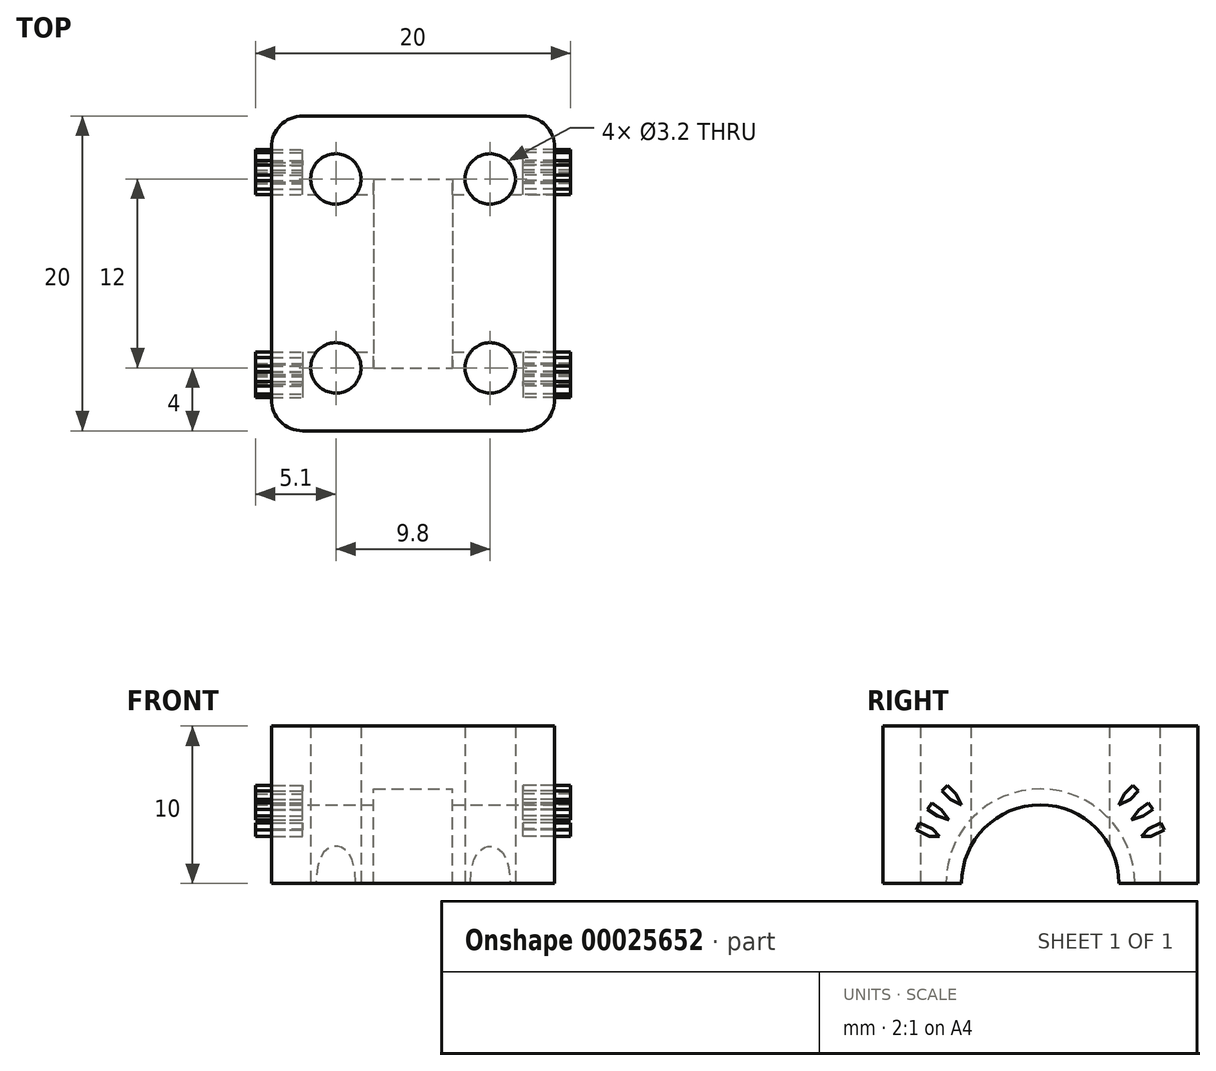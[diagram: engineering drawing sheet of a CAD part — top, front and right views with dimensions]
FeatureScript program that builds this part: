
annotation { "Feature Type Name" : "Feature", "Feature Type Description" : "" }
export const myFeature = defineFeature(function(context is Context, id is Id, definition is map)
    precondition{}
    {
        {
            var Q0;
            Q0=qCreatedBy(makeId("Top.planeOp"),FACE);
            var sketch = newSketch(context, id + "F0", { "sketchPlane" : qUnion([Q0])});
            skLineSegment(sketch, "E0.rect.bottom", {"start": v(4.9, -6) * mm, "end": v(-4.9, -6) * mm, "construction": true});
            skLineSegment(sketch, "E0.rect.top", {"start": v(4.9, 6) * mm, "end": v(-4.9, 6) * mm, "construction": true});
            skLineSegment(sketch, "E0.rect.left", {"start": v(4.9, -6) * mm, "end": v(4.9, 6) * mm, "construction": true});
            skLineSegment(sketch, "E0.rect.right", {"start": v(-4.9, -6) * mm, "end": v(-4.9, 6) * mm, "construction": true});
            skPoint(sketch, "E0.rect.middle", {"position": v(0, 0) * mm});
            skCircle(sketch, "E1", {"center": v(-4.9, 6) * mm, "radius": 1.6 * mm});
            skCircle(sketch, "E2.0.MirrorC", {"center": v(4.9, 6) * mm, "radius": 1.6 * mm});
            skCircle(sketch, "E3.0.MirrorC", {"center": v(-4.9, -6) * mm, "radius": 1.6 * mm});
            skCircle(sketch, "E4.0.MirrorC", {"center": v(4.9, -6) * mm, "radius": 1.6 * mm});
            skLineSegment(sketch, "E5.rect.bottom", {"start": v(-12.29, 4) * mm, "end": v(12.29, 4) * mm, "construction": true});
            skLineSegment(sketch, "E5.rect.top", {"start": v(-12.29, -4) * mm, "end": v(12.29, -4) * mm, "construction": true});
            skLineSegment(sketch, "E6.rect.bottom", {"start": v(7, -10) * mm, "end": v(-7, -10) * mm});
            skLineSegment(sketch, "E6.rect.top", {"start": v(7, 10) * mm, "end": v(-7, 10) * mm});
            skLineSegment(sketch, "E6.rect.left", {"start": v(9, -8) * mm, "end": v(9, 8) * mm});
            skLineSegment(sketch, "E6.rect.right", {"start": v(-9, -8) * mm, "end": v(-9, 8) * mm});
            skPoint(sketch, "E7.visualSharp", {"position": v(-9, 10) * mm});
            skArc(sketch, "E7.filletArc", {"start": v(-7, 10) * mm, "mid": v(-8.41, 9.41) * mm, "end": v(-9, 8) * mm});
            skPoint(sketch, "E8.visualSharp", {"position": v(9, 10) * mm});
            skArc(sketch, "E8.filletArc", {"start": v(9, 8) * mm, "mid": v(8.41, 9.41) * mm, "end": v(7, 10) * mm});
            skPoint(sketch, "E9.visualSharp", {"position": v(9, -10) * mm});
            skArc(sketch, "E9.filletArc", {"start": v(7, -10) * mm, "mid": v(8.41, -9.41) * mm, "end": v(9, -8) * mm});
            skPoint(sketch, "E10.visualSharp", {"position": v(-9, -10) * mm});
            skArc(sketch, "E10.filletArc", {"start": v(-9, -8) * mm, "mid": v(-8.41, -9.41) * mm, "end": v(-7, -10) * mm});
            skSolve(sketch);
        }
        {
            var Q0;
            Q0=qSketchRegion(id+"F0",true);
            extrude(context, id + "F1", {"entities" : qUnion([Q0]), "depth" : 10 * mm});
        }
        {
            var Q0;
            Q0=qCreatedBy(makeId("Front.planeOp"),FACE);
            var sketch = newSketch(context, id + "F2", { "sketchPlane" : qUnion([Q0])});
            skLineSegment(sketch, "E11", {"start": v(0, 0) * mm, "end": v(11.21, 0) * mm, "construction": true});
            skLineSegment(sketch, "E12", {"start": v(0, 0) * mm, "end": v(-12.6, 0) * mm, "construction": true});
            skLineSegment(sketch, "E13", {"start": v(-9.87, 0) * mm, "end": v(-9.87, 5) * mm});
            skLineSegment(sketch, "E14", {"start": v(-9.87, 5) * mm, "end": v(-2.5, 5) * mm});
            skLineSegment(sketch, "E15", {"start": v(-2.5, 5) * mm, "end": v(-2.5, 6) * mm});
            skLineSegment(sketch, "E16", {"start": v(-2.5, 6) * mm, "end": v(0, 6) * mm});
            skLineSegment(sketch, "E17", {"start": v(0, 0) * mm, "end": v(-9.87, 0) * mm});
            skLineSegment(sketch, "E18", {"start": v(0, 0) * mm, "end": v(0, 13.48) * mm, "construction": true});
            skLineSegment(sketch, "E19.0.MirrorCS", {"start": v(2.5, 6) * mm, "end": v(0, 6) * mm});
            skLineSegment(sketch, "E20.0.MirrorCS", {"start": v(2.5, 5) * mm, "end": v(2.5, 6) * mm});
            skLineSegment(sketch, "E21.0.MirrorCS", {"start": v(9.87, 5) * mm, "end": v(2.5, 5) * mm});
            skLineSegment(sketch, "E22.0.MirrorCS", {"start": v(9.87, 0) * mm, "end": v(9.87, 5) * mm});
            skLineSegment(sketch, "E23.0.MirrorCS", {"start": v(0, 0) * mm, "end": v(9.87, 0) * mm});
            skSolve(sketch);
        }
        {
            var Q0;
            Q0=makeQuery(id+"F2.imprint","IMPRINT",FACE,{"disambiguationData":[TD([[makeQuery(id+"F2.imprint","IMPRINT",EDGE,{"derivedFrom":sQuery(id+"F2.wireOp",EDGE,"E13")}),-1.0]])]});
            var Q1;
            Q1=sQuery(id+"F2.wireOp",EDGE,"E12");
            revolve(context, id + "F3", {"entities" : qUnion([Q0]), "axis" : qUnion([Q1]), "revolveType" : RevolveType.FULL});
        }
        {
            var Q0;
            Q0=makeQuery(id+"F3.opRevolve","SWEPT_BODY",BODY,{"disambiguationData":[OSD([sQuery(id+"F2.wireOp",EDGE,"E13"),sQuery(id+"F2.wireOp",EDGE,"E14"),sQuery(id+"F2.wireOp",EDGE,"E15"),sQuery(id+"F2.wireOp",EDGE,"E16"),sQuery(id+"F2.wireOp",EDGE,"E17"),sQuery(id+"F2.wireOp",EDGE,"E19.0.MirrorCS"),sQuery(id+"F2.wireOp",EDGE,"E20.0.MirrorCS"),sQuery(id+"F2.wireOp",EDGE,"E21.0.MirrorCS"),sQuery(id+"F2.wireOp",EDGE,"E22.0.MirrorCS"),sQuery(id+"F2.wireOp",EDGE,"E23.0.MirrorCS")])]});
            var Q1;
            Q1=makeQuery(id+"F1.opExtrude","SWEPT_BODY",BODY,{"disambiguationData":[OSD([sQuery(id+"F0.wireOp",EDGE,"E1"),sQuery(id+"F0.wireOp",EDGE,"E2.0.MirrorC"),sQuery(id+"F0.wireOp",EDGE,"E3.0.MirrorC"),sQuery(id+"F0.wireOp",EDGE,"E4.0.MirrorC"),sQuery(id+"F0.wireOp",EDGE,"e5631a11-bc9c-4a52-adc7-c46cd8f11f6b"),sQuery(id+"F0.wireOp",EDGE,"bd637b92-1d0b-446d-8915-1d70d333add2.0.MirrorCS"),sQuery(id+"F0.wireOp",EDGE,"06c50760-1331-4ed2-a7b0-091f787a3063"),sQuery(id+"F0.wireOp",EDGE,"de07cfb3-cb16-40ab-bb82-3127aa1393aa"),sQuery(id+"F0.wireOp",EDGE,"04999754-2a12-4e44-a85a-65a4e2ceeff6"),sQuery(id+"F0.wireOp",EDGE,"dadc4557-2f52-4a31-bb1e-40eb43539002"),sQuery(id+"F0.wireOp",EDGE,"8e725be4-5807-46b2-9b6e-bd76df486bfe"),sQuery(id+"F0.wireOp",EDGE,"98050970-c6e9-4b0a-98d8-9d9cee821ab9"),sQuery(id+"F0.wireOp",EDGE,"6ad0ad36-7af7-4ad4-b520-2d92bf48e3fd"),sQuery(id+"F0.wireOp",EDGE,"b438de05-f02d-4cf3-920c-0279d859b767"),sQuery(id+"F0.wireOp",EDGE,"d851b83f-9951-4aca-81a3-513ac486d921"),sQuery(id+"F0.wireOp",EDGE,"5981cd49-f631-4702-ace7-539b31d2d0b1"),sQuery(id+"F0.wireOp",EDGE,"dddef0f6-cba6-4fc5-84df-45972f3e2711.filletArc"),sQuery(id+"F0.wireOp",EDGE,"58242231-5e53-4480-9a1e-0624a7f1f4e7.filletArc"),sQuery(id+"F0.wireOp",EDGE,"b5da0da3-f109-4bb3-8592-48b764635490.filletArc"),sQuery(id+"F0.wireOp",EDGE,"02dcfeaf-069a-4237-823f-dfffc468ed8a.filletArc")])]});
            booleanBodies(context, id + "F4", {"operationType" : BooleanOperationType.SUBTRACTION, "tools" : qUnion([Q0]), "targets" : qUnion([Q1])});
        }
        {
            var Q0;
            Q0=qCreatedBy(makeId("Right.planeOp"),FACE);
            var sketch = newSketch(context, id + "F5", { "sketchPlane" : qUnion([Q0])});
            skLineSegment(sketch, "E24.rect.bottom", {"start": v(5, -5) * mm, "end": v(-5, -5) * mm, "construction": true});
            skLineSegment(sketch, "E24.rect.top", {"start": v(5, 5) * mm, "end": v(-5, 5) * mm, "construction": true});
            skLineSegment(sketch, "E24.rect.left", {"start": v(5, -5) * mm, "end": v(5, 5) * mm, "construction": true});
            skLineSegment(sketch, "E24.rect.right", {"start": v(-5, -5) * mm, "end": v(-5, 5) * mm, "construction": true});
            skPoint(sketch, "E24.rect.middle", {"position": v(0, 0) * mm});
            skLineSegment(sketch, "E25", {"start": v(0, 0) * mm, "end": v(-6.64, 6.64) * mm, "construction": true});
            skLineSegment(sketch, "E26", {"start": v(0, 0) * mm, "end": v(-5.8, 4.06) * mm, "construction": true});
            skLineSegment(sketch, "E27", {"start": v(0, 0) * mm, "end": v(-5.42, 4.55) * mm, "construction": true});
            skLineSegment(sketch, "E28", {"start": v(0, 0) * mm, "end": v(-6.12, 3.54) * mm, "construction": true});
            skLineSegment(sketch, "E29", {"start": v(0, 0) * mm, "end": v(-6.4, 2.99) * mm, "construction": true});
            skLineSegment(sketch, "E30", {"start": v(0, 0) * mm, "end": v(-5, 5) * mm});
            skLineSegment(sketch, "E31", {"start": v(0, 0) * mm, "end": v(-6.29, 7.92) * mm, "construction": true});
            skLineSegment(sketch, "E32", {"start": v(0, 0) * mm, "end": v(0, 0.41) * mm, "construction": true});
            skLineSegment(sketch, "E33", {"start": v(-5, 5) * mm, "end": v(-6.06, 6.06) * mm});
            skLineSegment(sketch, "E34", {"start": v(-5.8, 4.06) * mm, "end": v(-7.02, 4.92) * mm});
            skLineSegment(sketch, "E35", {"start": v(-6.4, 2.99) * mm, "end": v(-7.77, 3.62) * mm});
            skLineSegment(sketch, "E36.0", {"start": v(-5.35, 5.7) * mm, "end": v(-5.88, 6.24) * mm});
            skLineSegment(sketch, "E37.0", {"start": v(-5.7, 5.35) * mm, "end": v(-6.24, 5.88) * mm});
            skLineSegment(sketch, "E38", {"start": v(-5.88, 6.24) * mm, "end": v(-6.24, 5.88) * mm});
            skLineSegment(sketch, "E39", {"start": v(-5, 5) * mm, "end": v(-5.35, 5.7) * mm});
            skLineSegment(sketch, "E40", {"start": v(-5, 5) * mm, "end": v(-5.7, 5.35) * mm});
            skLineSegment(sketch, "E41", {"start": v(-5.42, 4.55) * mm, "end": v(-5.46, 4.59) * mm});
            skLineSegment(sketch, "E42", {"start": v(0, 0) * mm, "end": v(0, 8.3) * mm, "construction": true});
            skLineSegment(sketch, "E43.0.MirrorCS", {"start": v(5.35, 5.7) * mm, "end": v(5.88, 6.24) * mm});
            skLineSegment(sketch, "E44.0.MirrorCS", {"start": v(5.7, 5.35) * mm, "end": v(6.24, 5.88) * mm});
            skLineSegment(sketch, "E45.0.MirrorCS", {"start": v(5.88, 6.24) * mm, "end": v(6.24, 5.88) * mm});
            skLineSegment(sketch, "E46.0.MirrorCS", {"start": v(5, 5) * mm, "end": v(5.7, 5.35) * mm});
            skLineSegment(sketch, "E47.0.MirrorCS", {"start": v(5, 5) * mm, "end": v(5.35, 5.7) * mm});
            skLineSegment(sketch, "E48.0", {"start": v(-6.26, 4.7) * mm, "end": v(-6.88, 5.12) * mm});
            skLineSegment(sketch, "E49.0", {"start": v(-6.55, 4.28) * mm, "end": v(-7.16, 4.71) * mm});
            skLineSegment(sketch, "E50", {"start": v(-5.8, 4.06) * mm, "end": v(-6.26, 4.7) * mm});
            skLineSegment(sketch, "E51", {"start": v(-5.8, 4.06) * mm, "end": v(-6.55, 4.28) * mm});
            skLineSegment(sketch, "E52", {"start": v(-7.16, 4.71) * mm, "end": v(-6.88, 5.12) * mm});
            skPoint(sketch, "E53.orphan", {"position": v(-6.25, 3.32) * mm});
            skPoint(sketch, "E54.orphan", {"position": v(-6, 3.75) * mm});
            skLineSegment(sketch, "E55.0.MirrorCS", {"start": v(6.26, 4.7) * mm, "end": v(6.88, 5.12) * mm});
            skLineSegment(sketch, "E56.0.MirrorCS", {"start": v(6.55, 4.28) * mm, "end": v(7.16, 4.71) * mm});
            skLineSegment(sketch, "E57.0.MirrorCS", {"start": v(7.16, 4.71) * mm, "end": v(6.88, 5.12) * mm});
            skLineSegment(sketch, "E58.0.MirrorCS", {"start": v(5.8, 4.06) * mm, "end": v(6.55, 4.28) * mm});
            skLineSegment(sketch, "E59.0.MirrorCS", {"start": v(5.8, 4.06) * mm, "end": v(6.26, 4.7) * mm});
            skLineSegment(sketch, "E60.0", {"start": v(-6.85, 3.47) * mm, "end": v(-7.66, 3.85) * mm});
            skLineSegment(sketch, "E61.0", {"start": v(-7.03, 3) * mm, "end": v(-7.87, 3.4) * mm});
            skLineSegment(sketch, "E62", {"start": v(-7.66, 3.85) * mm, "end": v(-7.87, 3.4) * mm});
            skLineSegment(sketch, "E63", {"start": v(-6.4, 2.99) * mm, "end": v(-6.85, 3.47) * mm});
            skLineSegment(sketch, "E64", {"start": v(-6.4, 2.99) * mm, "end": v(-7.03, 3) * mm});
            skLineSegment(sketch, "E65.0.MirrorCS", {"start": v(6.85, 3.47) * mm, "end": v(7.66, 3.85) * mm});
            skLineSegment(sketch, "E66.0.MirrorCS", {"start": v(7.66, 3.85) * mm, "end": v(7.87, 3.4) * mm});
            skLineSegment(sketch, "E67.0.MirrorCS", {"start": v(7.03, 3) * mm, "end": v(7.87, 3.4) * mm});
            skLineSegment(sketch, "E68.0.MirrorCS", {"start": v(6.4, 2.99) * mm, "end": v(7.03, 3) * mm});
            skLineSegment(sketch, "E69.0.MirrorCS", {"start": v(6.4, 2.99) * mm, "end": v(6.85, 3.47) * mm});
            skSolve(sketch);
        }
        {
            var Q0;
            Q0=qSketchRegion(id+"F5",true);
            extrude(context, id + "F6", {"entities" : qUnion([Q0]), "depth" : 3 * mm});
        }
        {
            var Q0;
            Q0=makeQuery(id+"F6.opExtrude","SWEPT_BODY",BODY,{"disambiguationData":[OSD([sQuery(id+"F5.wireOp",EDGE,"E60.0"),sQuery(id+"F5.wireOp",EDGE,"E61.0"),sQuery(id+"F5.wireOp",EDGE,"E62"),sQuery(id+"F5.wireOp",EDGE,"E63"),sQuery(id+"F5.wireOp",EDGE,"E64")])]});
            var Q1;
            Q1=makeQuery(id+"F6.opExtrude","SWEPT_BODY",BODY,{"disambiguationData":[OSD([sQuery(id+"F5.wireOp",EDGE,"E48.0"),sQuery(id+"F5.wireOp",EDGE,"E49.0"),sQuery(id+"F5.wireOp",EDGE,"E50"),sQuery(id+"F5.wireOp",EDGE,"E51"),sQuery(id+"F5.wireOp",EDGE,"E52")])]});
            var Q2;
            Q2=makeQuery(id+"F6.opExtrude","SWEPT_BODY",BODY,{"disambiguationData":[OSD([sQuery(id+"F5.wireOp",EDGE,"E36.0"),sQuery(id+"F5.wireOp",EDGE,"E37.0"),sQuery(id+"F5.wireOp",EDGE,"E38"),sQuery(id+"F5.wireOp",EDGE,"E39"),sQuery(id+"F5.wireOp",EDGE,"E40")])]});
            var Q3;
            Q3=makeQuery(id+"F6.opExtrude","SWEPT_BODY",BODY,{"disambiguationData":[OSD([sQuery(id+"F5.wireOp",EDGE,"E43.0.MirrorCS"),sQuery(id+"F5.wireOp",EDGE,"E44.0.MirrorCS"),sQuery(id+"F5.wireOp",EDGE,"E45.0.MirrorCS"),sQuery(id+"F5.wireOp",EDGE,"E46.0.MirrorCS"),sQuery(id+"F5.wireOp",EDGE,"E47.0.MirrorCS")])]});
            var Q4;
            Q4=makeQuery(id+"F6.opExtrude","SWEPT_BODY",BODY,{"disambiguationData":[OSD([sQuery(id+"F5.wireOp",EDGE,"E65.0.MirrorCS"),sQuery(id+"F5.wireOp",EDGE,"E66.0.MirrorCS"),sQuery(id+"F5.wireOp",EDGE,"E67.0.MirrorCS"),sQuery(id+"F5.wireOp",EDGE,"E68.0.MirrorCS"),sQuery(id+"F5.wireOp",EDGE,"E69.0.MirrorCS")])]});
            var Q5;
            Q5=makeQuery(id+"F6.opExtrude","SWEPT_BODY",BODY,{"disambiguationData":[OSD([sQuery(id+"F5.wireOp",EDGE,"E55.0.MirrorCS"),sQuery(id+"F5.wireOp",EDGE,"E56.0.MirrorCS"),sQuery(id+"F5.wireOp",EDGE,"E57.0.MirrorCS"),sQuery(id+"F5.wireOp",EDGE,"E58.0.MirrorCS"),sQuery(id+"F5.wireOp",EDGE,"E59.0.MirrorCS")])]});
            var Q6;
            Q6=makeQuery(id+"F1.opExtrude","SWEPT_FACE",FACE,{"disambiguationData":[OSD([sQuery(id+"F0.wireOp",EDGE,"E6.rect.left")])]});
            transform(context, id + "F7", {"entities" : qUnion([Q0, Q1, Q2, Q3, Q4, Q5]), "transformType" : TransformType.TRANSLATION_DISTANCE, "transformDirection" : qUnion([Q6]), "distance" : 7 * mm, "makeCopy" : false});
        }
        {
            var Q0;
            Q0=qSketchRegion(id+"F5",true);
            extrude(context, id + "F8", {"entities" : qUnion([Q0]), "oppositeDirection" : true, "depth" : 3 * mm});
        }
        {
            var Q0;
            Q0=makeQuery(id+"F8.opExtrude","SWEPT_BODY",BODY,{"disambiguationData":[OSD([sQuery(id+"F5.wireOp",EDGE,"E36.0"),sQuery(id+"F5.wireOp",EDGE,"E37.0"),sQuery(id+"F5.wireOp",EDGE,"E38"),sQuery(id+"F5.wireOp",EDGE,"E39"),sQuery(id+"F5.wireOp",EDGE,"E40")])]});
            var Q1;
            Q1=makeQuery(id+"F8.opExtrude","SWEPT_BODY",BODY,{"disambiguationData":[OSD([sQuery(id+"F5.wireOp",EDGE,"E43.0.MirrorCS"),sQuery(id+"F5.wireOp",EDGE,"E44.0.MirrorCS"),sQuery(id+"F5.wireOp",EDGE,"E45.0.MirrorCS"),sQuery(id+"F5.wireOp",EDGE,"E46.0.MirrorCS"),sQuery(id+"F5.wireOp",EDGE,"E47.0.MirrorCS")])]});
            var Q2;
            Q2=makeQuery(id+"F8.opExtrude","SWEPT_BODY",BODY,{"disambiguationData":[OSD([sQuery(id+"F5.wireOp",EDGE,"E48.0"),sQuery(id+"F5.wireOp",EDGE,"E49.0"),sQuery(id+"F5.wireOp",EDGE,"E50"),sQuery(id+"F5.wireOp",EDGE,"E51"),sQuery(id+"F5.wireOp",EDGE,"E52")])]});
            var Q3;
            Q3=makeQuery(id+"F8.opExtrude","SWEPT_BODY",BODY,{"disambiguationData":[OSD([sQuery(id+"F5.wireOp",EDGE,"E55.0.MirrorCS"),sQuery(id+"F5.wireOp",EDGE,"E56.0.MirrorCS"),sQuery(id+"F5.wireOp",EDGE,"E57.0.MirrorCS"),sQuery(id+"F5.wireOp",EDGE,"E58.0.MirrorCS"),sQuery(id+"F5.wireOp",EDGE,"E59.0.MirrorCS")])]});
            var Q4;
            Q4=makeQuery(id+"F8.opExtrude","SWEPT_BODY",BODY,{"disambiguationData":[OSD([sQuery(id+"F5.wireOp",EDGE,"E60.0"),sQuery(id+"F5.wireOp",EDGE,"E61.0"),sQuery(id+"F5.wireOp",EDGE,"E62"),sQuery(id+"F5.wireOp",EDGE,"E63"),sQuery(id+"F5.wireOp",EDGE,"E64")])]});
            var Q5;
            Q5=makeQuery(id+"F8.opExtrude","SWEPT_BODY",BODY,{"disambiguationData":[OSD([sQuery(id+"F5.wireOp",EDGE,"E65.0.MirrorCS"),sQuery(id+"F5.wireOp",EDGE,"E66.0.MirrorCS"),sQuery(id+"F5.wireOp",EDGE,"E67.0.MirrorCS"),sQuery(id+"F5.wireOp",EDGE,"E68.0.MirrorCS"),sQuery(id+"F5.wireOp",EDGE,"E69.0.MirrorCS")])]});
            var Q6;
            Q6=makeQuery(id+"F1.opExtrude","SWEPT_FACE",FACE,{"disambiguationData":[OSD([sQuery(id+"F0.wireOp",EDGE,"E6.rect.right")])]});
            transform(context, id + "F9", {"entities" : qUnion([Q0, Q1, Q2, Q3, Q4, Q5]), "transformType" : TransformType.TRANSLATION_DISTANCE, "transformDirection" : qUnion([Q6]), "distance" : 7 * mm, "makeCopy" : false});
        }
    });
